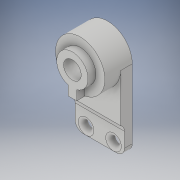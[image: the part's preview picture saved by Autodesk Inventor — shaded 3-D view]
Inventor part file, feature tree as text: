
AUTODESK INVENTOR PART (.ipt)
format: ipt  version: 2019 (Build 230136000, 136)  size: 396,288 bytes
history: native  units: in
note: dims shown in document units (in); Inventor stores cm internally (conversion verified against a paired STEP export)
features: extrude x5, sketch x5, fillet x4
ambient origin geometry x8: Origin, YZ Plane, XZ Plane, XY Plane, X Axis, Y Axis, Z Axis, Center Point
bodies: Solid1 (feature_tree)
feature tree (14):
  extrude  "Extrusion1"  Depth=0.63in
  extrude  "Extrusion2"  Depth=0.15in TaperAngle=0.0deg
  extrude  "Extrusion3"  Depth=0.4in
  extrude  "Extrusion5"  Depth=0.111in
  extrude  "Extrusion4"  Depth=0.1in
  fillet  "Fillet1"  Radius=0.1in
  fillet  "Fillet2"  Radius=0.1in
  fillet  "Fillet3"  Radius=0.35in
  fillet  "Fillet4"  Radius=0.1in
  sketch  "Sketch1"  dims[d0=0.32in d1=0.63in]
  sketch  "Sketch2"  dims[d2=1.3in d3=0.15in d4=0.0in]
  sketch  "Sketch3"  dims[d5=0.225in d6=0.4in]
  sketch  "Sketch4"  dims[d7=0.111in d8=0.515in]
  sketch  "Sketch5"  dims[d9=0.3in d10=0.0in d11=0.1in d12=0.1in d13=0.1in d14=0.35in d15=0.1in d16=0.3in d17=0.0in d18=0.375in d19=0.05in d20=0.0in d21=0.2in d22=0.0in]
